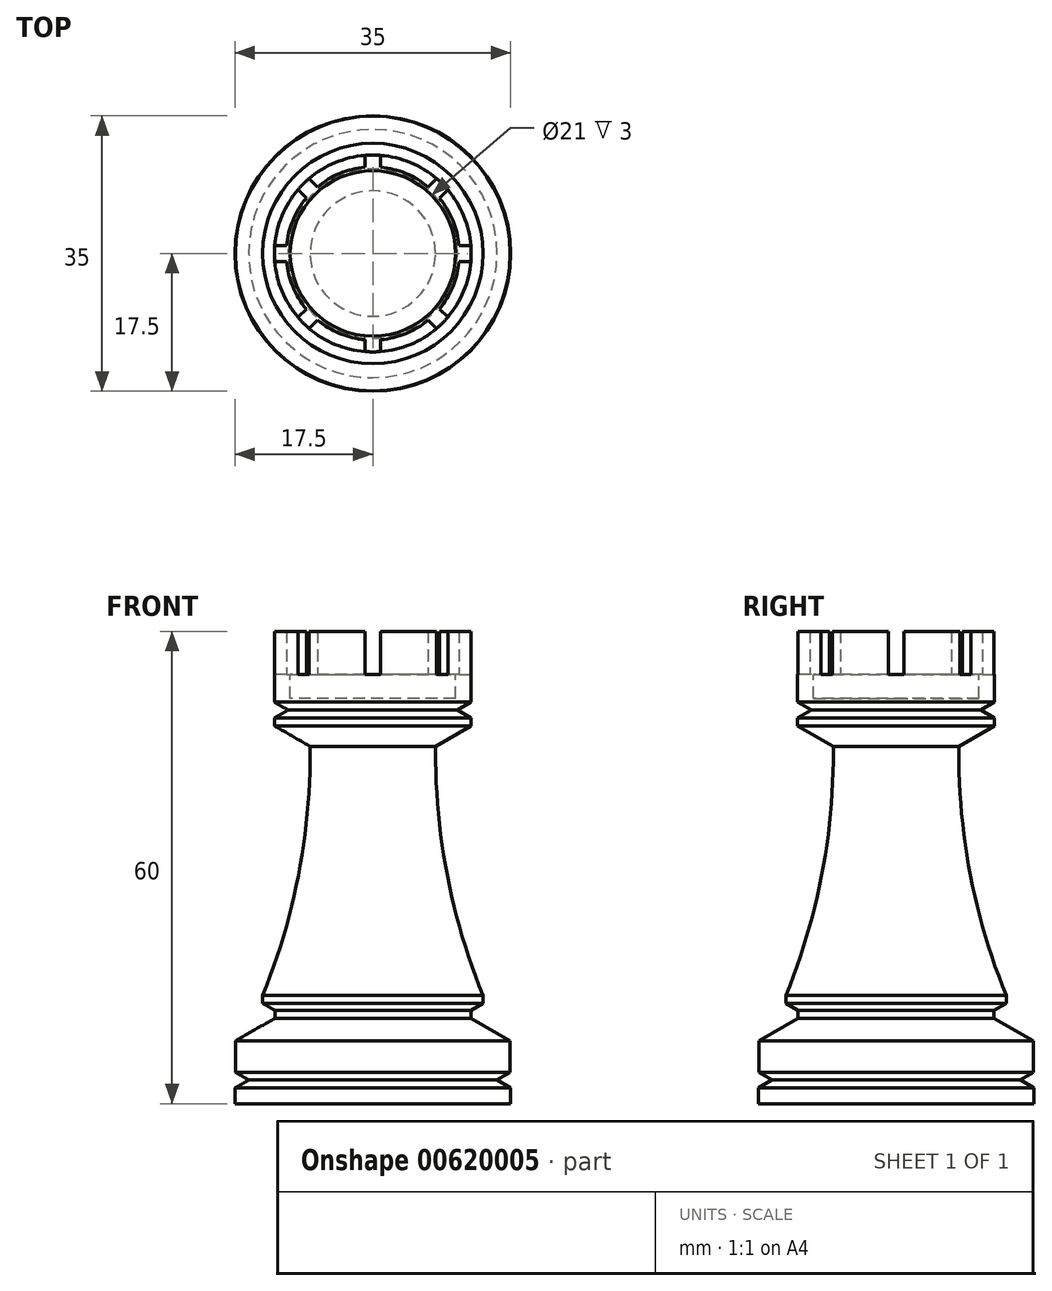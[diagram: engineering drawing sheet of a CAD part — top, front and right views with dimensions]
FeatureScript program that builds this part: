
annotation { "Feature Type Name" : "Feature", "Feature Type Description" : "" }
export const myFeature = defineFeature(function(context is Context, id is Id, definition is map)
    precondition{}
    {
        {
            var Q0;
            Q0=qCreatedBy(makeId("Front.planeOp"),FACE);
            var sketch = newSketch(context, id + "F0", { "sketchPlane" : qUnion([Q0])});
            skLineSegment(sketch, "E0", {"start": v(0, 0) * mm, "end": v(17.5, 0) * mm});
            skLineSegment(sketch, "E1", {"start": v(17.5, 0) * mm, "end": v(17.5, 2) * mm});
            skLineSegment(sketch, "E2", {"start": v(17.45, 3.97) * mm, "end": v(17.45, 7.97) * mm});
            skLineSegment(sketch, "E3", {"start": v(17.5, 2) * mm, "end": v(15.77, 3) * mm});
            skLineSegment(sketch, "E4", {"start": v(15.77, 3) * mm, "end": v(17.45, 3.97) * mm});
            skLineSegment(sketch, "E5", {"start": v(0, 0) * mm, "end": v(0, 6) * mm});
            skLineSegment(sketch, "E6", {"start": v(17.45, 7.97) * mm, "end": v(12.45, 10.86) * mm});
            skLineSegment(sketch, "E7.0", {"start": v(11, 60) * mm, "end": v(12.5, 60) * mm});
            skLineSegment(sketch, "E8.0", {"start": v(12.5, 60) * mm, "end": v(12.5, 51) * mm});
            skPoint(sketch, "E9.end.orphan", {"position": v(17.5, 3) * mm});
            skLineSegment(sketch, "E10.0", {"start": v(7.98, 43.46) * mm, "end": v(7.96, 45.38) * mm});
            skLineSegment(sketch, "E11", {"start": v(12.5, 48) * mm, "end": v(7.96, 45.38) * mm});
            skLineSegment(sketch, "E12", {"start": v(12.5, 49) * mm, "end": v(10.77, 50) * mm});
            skLineSegment(sketch, "E13", {"start": v(10.77, 50) * mm, "end": v(12.5, 51) * mm});
            skLineSegment(sketch, "E14.trimOffspring", {"start": v(12.5, 49) * mm, "end": v(12.5, 48) * mm});
            skPoint(sketch, "E15.visualSharp", {"position": v(7.98, 43.46) * mm});
            skPoint(sketch, "E16.orphan", {"position": v(0, 6) * mm});
            skLineSegment(sketch, "E17", {"start": v(0, 0) * mm, "end": v(0, 60) * mm});
            skLineSegment(sketch, "E18.0", {"start": v(0, 54.5) * mm, "end": v(11, 54.5) * mm});
            skLineSegment(sketch, "E19.0", {"start": v(11, 60) * mm, "end": v(11, 54.5) * mm});
            skLineSegment(sketch, "E20.0", {"start": v(12.45, 10.86) * mm, "end": v(12.45, 11.86) * mm});
            skLineSegment(sketch, "E21", {"start": v(12.45, 11.86) * mm, "end": v(14, 12.75) * mm});
            skLineSegment(sketch, "E22.0", {"start": v(14, 12.75) * mm, "end": v(14, 13.75) * mm});
            skPoint(sketch, "E23.end.orphan", {"position": v(0, 40.68) * mm});
            skPoint(sketch, "E24.3.internal.snap0", {"position": v(14.95, 9.41) * mm});
            skArc(sketch, "E25", {"start": v(7.98, 43.46) * mm, "mid": v(9.59, 28.32) * mm, "end": v(14, 13.75) * mm});
            skSolve(sketch);
        }
        {
            var Q0;
            {var subQ1=sQuery(id+"F0.wireOp",EDGE,"E0");Q0=makeQuery(id+"F0.imprint","IMPRINT",FACE,{"disambiguationData":[TD([[makeQuery(id+"F0.imprint","IMPRINT",EDGE,{"derivedFrom":subQ1}),1.0]])]});}
            var Q1;
            Q1=sQuery(id+"F0.wireOp",EDGE,"E17");
            revolve(context, id + "F1", {"entities" : qUnion([Q0]), "axis" : qUnion([Q1]), "revolveType" : RevolveType.FULL});
        }
        {
            var Q0;
            Q0=makeQuery(id+"F1.opRevolve","SWEPT_FACE",FACE,{"disambiguationData":[OSD([sQuery(id+"F0.wireOp",EDGE,"E18.0")])]});
            var sketch = newSketch(context, id + "F2", { "sketchPlane" : qUnion([Q0])});
            skLineSegment(sketch, "E26", {"start": v(0, 0) * mm, "end": v(33.12, 0) * mm});
            skLineSegment(sketch, "E27.0", {"start": v(0.41, -1) * mm, "end": v(33.12, -1) * mm});
            skLineSegment(sketch, "E28.0", {"start": v(0, 1) * mm, "end": v(33.12, 1) * mm});
            skLineSegment(sketch, "E29", {"start": v(0, 1) * mm, "end": v(-22.42, 1) * mm});
            skLineSegment(sketch, "E30", {"start": v(-22.42, 1) * mm, "end": v(-22.42, -1) * mm});
            skLineSegment(sketch, "E31", {"start": v(-22.42, -1) * mm, "end": v(0.41, -1) * mm});
            skLineSegment(sketch, "E32", {"start": v(33.12, 1) * mm, "end": v(33.12, -1) * mm});
            skLineSegment(sketch, "E33", {"start": v(0, 0) * mm, "end": v(0, 23.98) * mm});
            skLineSegment(sketch, "E34", {"start": v(0, 23.98) * mm, "end": v(-1, 23.98) * mm});
            skLineSegment(sketch, "E35", {"start": v(-1, 23.98) * mm, "end": v(-1, -22.24) * mm});
            skLineSegment(sketch, "E36", {"start": v(-1, -22.24) * mm, "end": v(1, -22.24) * mm});
            skLineSegment(sketch, "E37", {"start": v(1, -22.24) * mm, "end": v(1, 23.98) * mm});
            skLineSegment(sketch, "E38", {"start": v(1, 23.98) * mm, "end": v(0, 23.98) * mm});
            skLineSegment(sketch, "E39", {"start": v(0, 0) * mm, "end": v(21.43, 21.43) * mm});
            skLineSegment(sketch, "E40.0", {"start": v(0.7, -0.7) * mm, "end": v(22.14, 20.73) * mm});
            skLineSegment(sketch, "E41.0", {"start": v(-0.7, 0.7) * mm, "end": v(20.73, 22.14) * mm});
            skLineSegment(sketch, "E42", {"start": v(0.41, -1) * mm, "end": v(-22.47, -23.89) * mm});
            skLineSegment(sketch, "E43", {"start": v(-22.47, -23.89) * mm, "end": v(-23.89, -22.47) * mm});
            skLineSegment(sketch, "E44", {"start": v(-23.89, -22.47) * mm, "end": v(-0.7, 0.7) * mm});
            skLineSegment(sketch, "E45", {"start": v(20.73, 22.14) * mm, "end": v(22.14, 20.73) * mm});
            skLineSegment(sketch, "E46", {"start": v(0, 0) * mm, "end": v(-19.02, 19.02) * mm});
            skLineSegment(sketch, "E47", {"start": v(-18.31, 19.73) * mm, "end": v(21.43, -20.02) * mm});
            skLineSegment(sketch, "E48", {"start": v(21.43, -20.02) * mm, "end": v(20.02, -21.43) * mm});
            skLineSegment(sketch, "E49", {"start": v(20.02, -21.43) * mm, "end": v(-19.69, 18.27) * mm});
            skLineSegment(sketch, "E50", {"start": v(-19.69, 18.27) * mm, "end": v(-18.31, 19.73) * mm});
            skLineSegment(sketch, "E51", {"start": v(-18.31, 19.73) * mm, "end": v(-19.69, 18.27) * mm});
            skSolve(sketch);
        }
        {
            var Q0;
            Q0=qSketchRegion(id+"F2",true);
            extrude(context, id + "F3", {"entities" : qUnion([Q0]), "operationType" : NewBodyOperationType.REMOVE, "depth" : 27 * mm});
        }
        {
            var Q0;
            Q0=makeQuery(id+"F3.boolean.opBoolean","MERGE",FACE,{"derivedFrom":[makeQuery(id+"F1.opRevolve","SWEPT_FACE",FACE,{"disambiguationData":[OSD([sQuery(id+"F0.wireOp",EDGE,"E18.0")])]}),makeQuery(id+"F3.opExtrude","CAP_FACE",FACE,{"disambiguationData":[OSD([sQuery(id+"F2.wireOp",EDGE,"E27.0"),sQuery(id+"F2.wireOp",EDGE,"E28.0"),sQuery(id+"F2.wireOp",EDGE,"E29"),sQuery(id+"F2.wireOp",EDGE,"E30"),sQuery(id+"F2.wireOp",EDGE,"E31"),sQuery(id+"F2.wireOp",EDGE,"E32"),sQuery(id+"F2.wireOp",EDGE,"E34"),sQuery(id+"F2.wireOp",EDGE,"E35"),sQuery(id+"F2.wireOp",EDGE,"E36"),sQuery(id+"F2.wireOp",EDGE,"E37"),sQuery(id+"F2.wireOp",EDGE,"E38"),sQuery(id+"F2.wireOp",EDGE,"E40.0"),sQuery(id+"F2.wireOp",EDGE,"E41.0"),sQuery(id+"F2.wireOp",EDGE,"E42"),sQuery(id+"F2.wireOp",EDGE,"E43"),sQuery(id+"F2.wireOp",EDGE,"E44"),sQuery(id+"F2.wireOp",EDGE,"E47"),sQuery(id+"F2.wireOp",EDGE,"E48"),sQuery(id+"F2.wireOp",EDGE,"E49"),sQuery(id+"F2.wireOp",EDGE,"E45"),sQuery(id+"F2.wireOp",EDGE,"E51")])],"isStart":true})]});
            var sketch = newSketch(context, id + "F4", { "sketchPlane" : qUnion([Q0])});
            skCircle(sketch, "E52", {"center": v(0, 0) * mm, "radius": 10.5 * mm});
            skSolve(sketch);
        }
        {
            var Q0;
            Q0=qSketchRegion(id+"F4",true);
            extrude(context, id + "F5", {"entities" : qUnion([Q0]), "operationType" : NewBodyOperationType.REMOVE, "oppositeDirection" : true, "depth" : 3 * mm});
        }
    });
